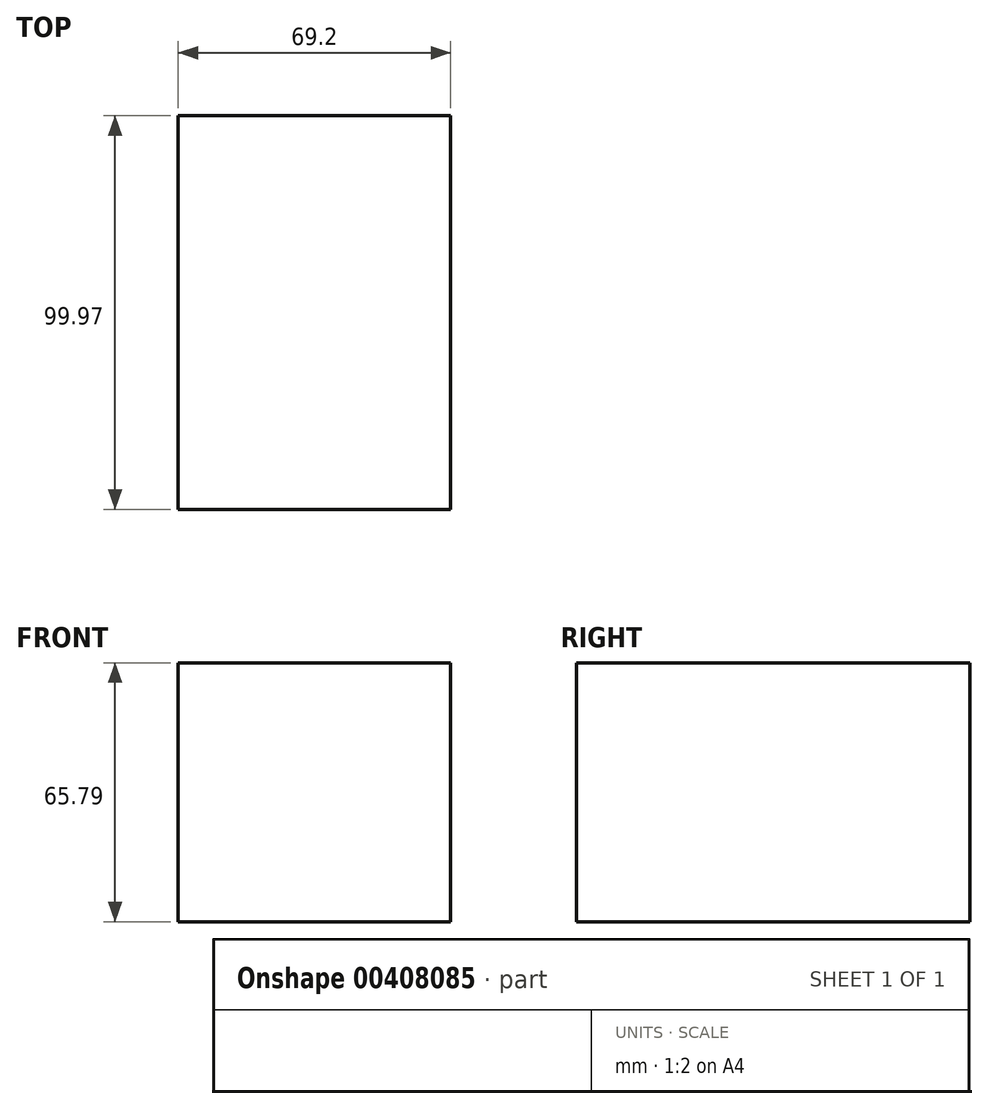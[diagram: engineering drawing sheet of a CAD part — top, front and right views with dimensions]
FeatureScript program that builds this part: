
annotation { "Feature Type Name" : "Feature", "Feature Type Description" : "" }
export const myFeature = defineFeature(function(context is Context, id is Id, definition is map)
    precondition{}
    {
        {
            var Q0;
            Q0=qCreatedBy(makeId("Top.planeOp"),FACE);
            var sketch = newSketch(context, id + "F0", { "sketchPlane" : qUnion([Q0])});
            skLineSegment(sketch, "E0.bottom", {"start": v(-33.53, 25.45) * mm, "end": v(35.67, 25.45) * mm});
            skLineSegment(sketch, "E0.top", {"start": v(-33.53, -74.52) * mm, "end": v(35.67, -74.52) * mm});
            skLineSegment(sketch, "E0.left", {"start": v(-33.53, 25.45) * mm, "end": v(-33.53, -74.52) * mm});
            skLineSegment(sketch, "E0.right", {"start": v(35.67, 25.45) * mm, "end": v(35.67, -74.52) * mm});
            skSolve(sketch);
        }
        {
            var Q0;
            Q0 = qSketchRegion(id + "F0", true);
            extrude(context, id + "F1", {"entities" : qUnion([Q0]), "depth" : 65.8 * mm});
        }
    });
